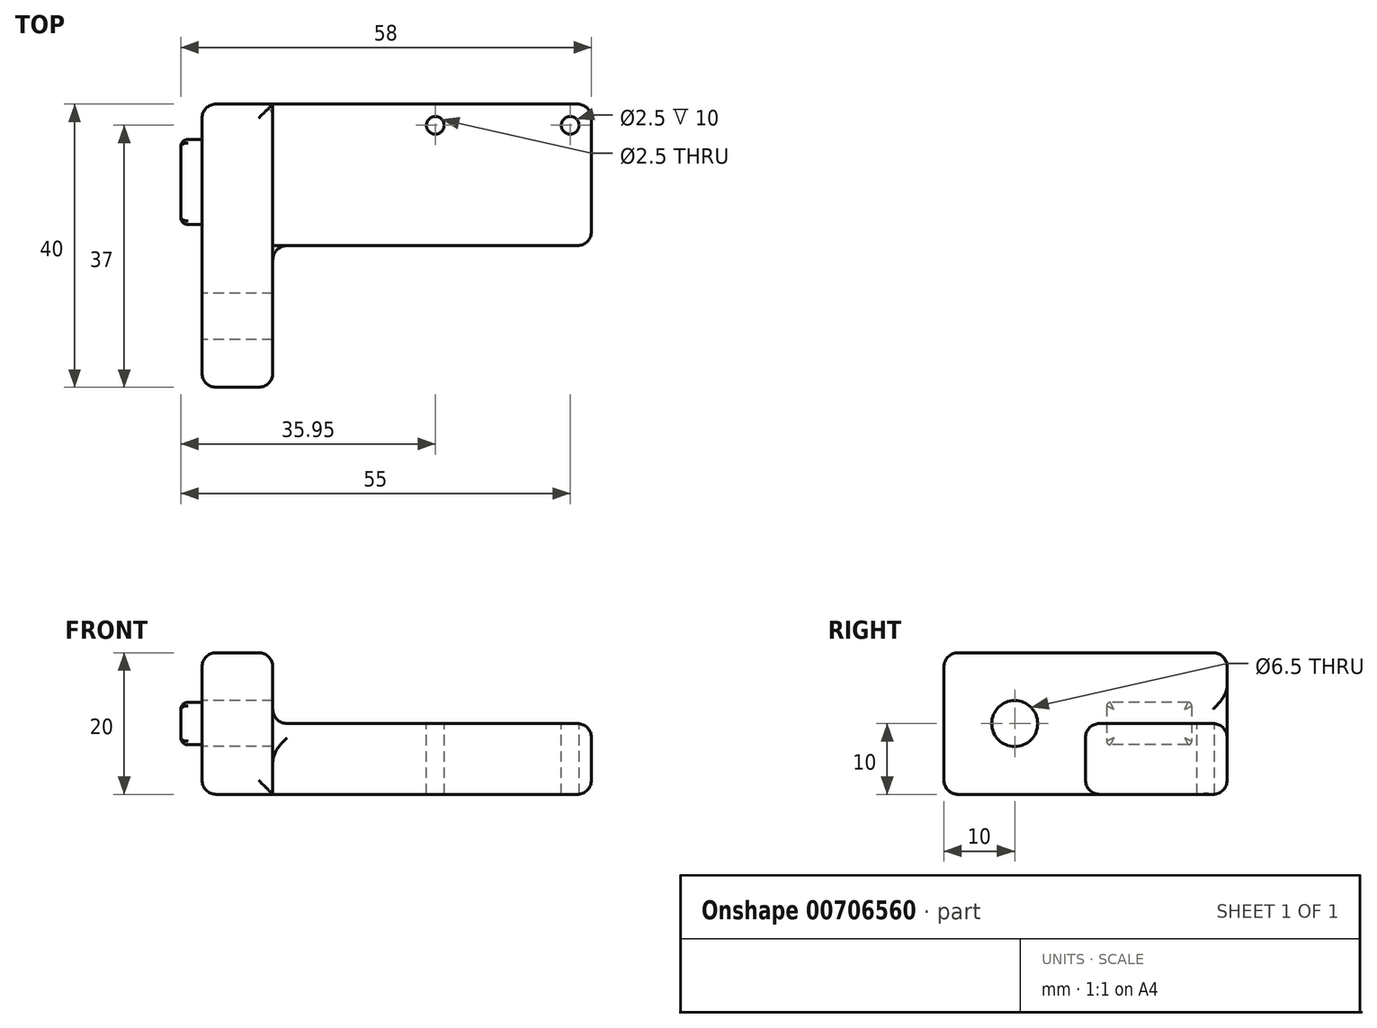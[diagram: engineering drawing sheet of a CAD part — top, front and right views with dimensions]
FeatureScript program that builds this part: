
annotation { "Feature Type Name" : "Feature", "Feature Type Description" : "" }
export const myFeature = defineFeature(function(context is Context, id is Id, definition is map)
    precondition{}
    {
        {
            var Q0;
            Q0=qCreatedBy(makeId("Top.planeOp"),FACE);
            var sketch = newSketch(context, id + "F0", { "sketchPlane" : qUnion([Q0])});
            skLineSegment(sketch, "E0.bottom", {"start": v(55, 20) * mm, "end": v(0, 20) * mm});
            skLineSegment(sketch, "E0.top", {"start": v(55, 0) * mm, "end": v(0, 0) * mm});
            skLineSegment(sketch, "E0.left", {"start": v(55, 20) * mm, "end": v(55, 0) * mm});
            skLineSegment(sketch, "E0.right", {"start": v(0, 20) * mm, "end": v(0, 0) * mm});
            skSolve(sketch);
        }
        {
            var Q0;
            Q0 = qSketchRegion(id + "F0", true);
            extrude(context, id + "F1", {"entities" : qUnion([Q0]), "depth" : 10 * mm, "offsetDistance" : 25 * mm});
        }
        {
            var Q0;
            Q0=makeQuery(id+"F1.opExtrude","CAP_FACE",FACE,{"disambiguationData":[OSD([sQuery(id+"F0.wireOp",EDGE,"E0.bottom"),sQuery(id+"F0.wireOp",EDGE,"E0.top"),sQuery(id+"F0.wireOp",EDGE,"E0.left"),sQuery(id+"F0.wireOp",EDGE,"E0.right")])],"isStart":false});
            var sketch = newSketch(context, id + "F2", { "sketchPlane" : qUnion([Q0])});
            skCircle(sketch, "E1", {"center": v(32.95, 17) * mm, "radius": 1.25 * mm});
            skCircle(sketch, "E2", {"center": v(52, 17) * mm, "radius": 1.25 * mm});
            skSolve(sketch);
        }
        {
            var Q0;
            Q0 = qSketchRegion(id + "F2", true);
            extrude(context, id + "F3", {"entities" : qUnion([Q0]), "operationType" : NewBodyOperationType.REMOVE, "oppositeDirection" : true, "depth" : 25 * mm, "offsetDistance" : 25 * mm});
        }
        {
            var Q0;
            Q0=makeQuery(id+"F1.opExtrude","SWEPT_FACE",FACE,{"disambiguationData":[OSD([sQuery(id+"F0.wireOp",EDGE,"E0.right")])]});
            var sketch = newSketch(context, id + "F4", { "sketchPlane" : qUnion([Q0])});
            skLineSegment(sketch, "E3.bottom", {"start": v(-20, 0) * mm, "end": v(20, 0) * mm});
            skLineSegment(sketch, "E3.top", {"start": v(-20, 20) * mm, "end": v(20, 20) * mm});
            skLineSegment(sketch, "E3.left", {"start": v(-20, 0) * mm, "end": v(-20, 20) * mm});
            skLineSegment(sketch, "E3.right", {"start": v(20, 0) * mm, "end": v(20, 20) * mm});
            skCircle(sketch, "E4", {"center": v(10, 10) * mm, "radius": 3.25 * mm});
            skSolve(sketch);
        }
        {
            var Q0;
            Q0 = qSketchRegion(id + "F4", true);
            extrude(context, id + "F5", {"entities" : qUnion([Q0]), "operationType" : NewBodyOperationType.ADD, "oppositeDirection" : true, "depth" : 10 * mm, "offsetDistance" : 25 * mm});
        }
        {
            var Q0;
            Q0=makeQuery(id+"F1.opExtrude","CAP_EDGE",EDGE,{"disambiguationData":[OSD([sQuery(id+"F0.wireOp",EDGE,"E0.top")])],"isStart":false});
            var Q1;
            Q1=makeQuery(id+"F1.opExtrude","CAP_EDGE",EDGE,{"disambiguationData":[OSD([sQuery(id+"F0.wireOp",EDGE,"E0.top")])],"isStart":true});
            var Q2;
            Q2=makeQuery(id+"F5.opExtrude","CAP_EDGE",EDGE,{"disambiguationData":[OSD([sQuery(id+"F4.wireOp",EDGE,"E3.top")])],"isStart":false});
            var Q3;
            Q3=makeQuery(id+"F5.boolean.opBoolean","INTERSECT",EDGE,{"derivedFrom":[makeQuery(id+"F1.opExtrude","CAP_FACE",FACE,{"disambiguationData":[OSD([sQuery(id+"F0.wireOp",EDGE,"E0.bottom"),sQuery(id+"F0.wireOp",EDGE,"E0.top"),sQuery(id+"F0.wireOp",EDGE,"E0.left"),sQuery(id+"F0.wireOp",EDGE,"E0.right")])],"isStart":false}),makeQuery(id+"F5.opExtrude","CAP_FACE",FACE,{"disambiguationData":[OSD([sQuery(id+"F4.wireOp",EDGE,"E3.bottom"),sQuery(id+"F4.wireOp",EDGE,"E3.top"),sQuery(id+"F4.wireOp",EDGE,"E3.left"),sQuery(id+"F4.wireOp",EDGE,"E3.right"),sQuery(id+"F4.wireOp",EDGE,"E4")])],"isStart":false})]});
            var Q4;
            Q4=makeQuery(id+"F1.opExtrude","CAP_EDGE",EDGE,{"disambiguationData":[OSD([sQuery(id+"F0.wireOp",EDGE,"E0.bottom")])],"isStart":false});
            var Q5;
            Q5=makeQuery(id+"F1.opExtrude","CAP_EDGE",EDGE,{"disambiguationData":[OSD([sQuery(id+"F0.wireOp",EDGE,"E0.bottom")])],"isStart":true});
            var Q6;
            Q6=makeQuery(id+"F5.opExtrude","SWEPT_EDGE",EDGE,{"disambiguationData":[OSD([sQuery(id+"F4.wireOp",EDGE,"E3.top"),sQuery(id+"F4.wireOp",EDGE,"E3.left")])]});
            var Q7;
            Q7=makeQuery(id+"F5.opExtrude","SWEPT_EDGE",EDGE,{"disambiguationData":[OSD([sQuery(id+"F4.wireOp",EDGE,"E3.bottom"),sQuery(id+"F4.wireOp",EDGE,"E3.right")])]});
            var Q8;
            Q8=makeQuery(id+"F5.opExtrude","CAP_EDGE",EDGE,{"disambiguationData":[OSD([sQuery(id+"F4.wireOp",EDGE,"E3.right")])],"isStart":false});
            var Q9;
            Q9=makeQuery(id+"F5.opExtrude","SWEPT_EDGE",EDGE,{"disambiguationData":[OSD([sQuery(id+"F4.wireOp",EDGE,"E3.top"),sQuery(id+"F4.wireOp",EDGE,"E3.right")])]});
            var Q10;
            Q10=makeQuery(id+"F1.opExtrude","SWEPT_FACE",FACE,{"disambiguationData":[OSD([sQuery(id+"F0.wireOp",EDGE,"E0.left")])]});
            fillet(context, id + "F6", {"entities" : qUnion([Q0, Q1, Q2, Q3, Q4, Q5, Q6, Q7, Q8, Q9, Q10]), "radius" : 2 * mm, "tangentPropagation" : true, "allowEdgeOverflow" : false});
        }
        {
            var Q0;
            Q0=makeQuery(id+"F5.boolean.opBoolean","MERGE",FACE,{"derivedFrom":[makeQuery(id+"F1.opExtrude","SWEPT_FACE",FACE,{"disambiguationData":[OSD([sQuery(id+"F0.wireOp",EDGE,"E0.right")])]}),makeQuery(id+"F5.opExtrude","CAP_FACE",FACE,{"disambiguationData":[OSD([sQuery(id+"F4.wireOp",EDGE,"E3.bottom"),sQuery(id+"F4.wireOp",EDGE,"E3.top"),sQuery(id+"F4.wireOp",EDGE,"E3.left"),sQuery(id+"F4.wireOp",EDGE,"E3.right"),sQuery(id+"F4.wireOp",EDGE,"E4")])],"isStart":true})]});
            var sketch = newSketch(context, id + "F7", { "sketchPlane" : qUnion([Q0])});
            skLineSegment(sketch, "E5.bottom", {"start": v(-15, 13) * mm, "end": v(-3, 13) * mm});
            skLineSegment(sketch, "E5.top", {"start": v(-15, 7) * mm, "end": v(-3, 7) * mm});
            skLineSegment(sketch, "E5.left", {"start": v(-15, 13) * mm, "end": v(-15, 7) * mm});
            skLineSegment(sketch, "E5.right", {"start": v(-3, 13) * mm, "end": v(-3, 7) * mm});
            skSolve(sketch);
        }
        {
            var Q0;
            Q0 = qSketchRegion(id + "F7", true);
            extrude(context, id + "F8", {"entities" : qUnion([Q0]), "operationType" : NewBodyOperationType.ADD, "depth" : 3 * mm, "offsetDistance" : 25 * mm});
        }
        {
            var Q0;
            Q0=makeQuery(id+"F8.opExtrude","CAP_EDGE",EDGE,{"disambiguationData":[OSD([sQuery(id+"F7.wireOp",EDGE,"E5.bottom")])],"isStart":true});
            var Q1;
            Q1=makeQuery(id+"F8.opExtrude","CAP_EDGE",EDGE,{"disambiguationData":[OSD([sQuery(id+"F7.wireOp",EDGE,"E5.right")])],"isStart":true});
            var Q2;
            Q2=makeQuery(id+"F8.opExtrude","CAP_EDGE",EDGE,{"disambiguationData":[OSD([sQuery(id+"F7.wireOp",EDGE,"E5.top")])],"isStart":true});
            var Q3;
            Q3=makeQuery(id+"F8.opExtrude","CAP_EDGE",EDGE,{"disambiguationData":[OSD([sQuery(id+"F7.wireOp",EDGE,"E5.left")])],"isStart":true});
            var Q4;
            Q4=makeQuery(id+"F8.opExtrude","SWEPT_EDGE",EDGE,{"disambiguationData":[OSD([sQuery(id+"F7.wireOp",EDGE,"E5.bottom"),sQuery(id+"F7.wireOp",EDGE,"E5.right")])]});
            var Q5;
            Q5=makeQuery(id+"F8.opExtrude","SWEPT_EDGE",EDGE,{"disambiguationData":[OSD([sQuery(id+"F7.wireOp",EDGE,"E5.bottom"),sQuery(id+"F7.wireOp",EDGE,"E5.left")])]});
            var Q6;
            Q6=makeQuery(id+"F8.opExtrude","SWEPT_EDGE",EDGE,{"disambiguationData":[OSD([sQuery(id+"F7.wireOp",EDGE,"E5.top"),sQuery(id+"F7.wireOp",EDGE,"E5.left")])]});
            var Q7;
            Q7=makeQuery(id+"F8.opExtrude","SWEPT_EDGE",EDGE,{"disambiguationData":[OSD([sQuery(id+"F7.wireOp",EDGE,"E5.top"),sQuery(id+"F7.wireOp",EDGE,"E5.right")])]});
            fillet(context, id + "F9", {"entities" : qUnion([Q0, Q1, Q2, Q3, Q4, Q5, Q6, Q7]), "radius" : .5 * mm, "tangentPropagation" : true, "allowEdgeOverflow" : false});
        }
        {
            var Q0;
            Q0=makeQuery(id+"F8.opExtrude","CAP_FACE",FACE,{"disambiguationData":[OSD([sQuery(id+"F7.wireOp",EDGE,"E5.bottom"),sQuery(id+"F7.wireOp",EDGE,"E5.top"),sQuery(id+"F7.wireOp",EDGE,"E5.left"),sQuery(id+"F7.wireOp",EDGE,"E5.right")])],"isStart":false});
            fillet(context, id + "F10", {"entities" : qUnion([Q0]), "radius" : 1 * mm, "tangentPropagation" : true, "allowEdgeOverflow" : false});
        }
        {
            var Q0;
            Q0=makeQuery(id+"F5.opExtrude","CAP_EDGE",EDGE,{"disambiguationData":[OSD([sQuery(id+"F4.wireOp",EDGE,"E3.top")])],"isStart":true});
            fillet(context, id + "F11", {"entities" : qUnion([Q0]), "radius" : 2 * mm, "tangentPropagation" : true, "allowEdgeOverflow" : false});
        }
    });
